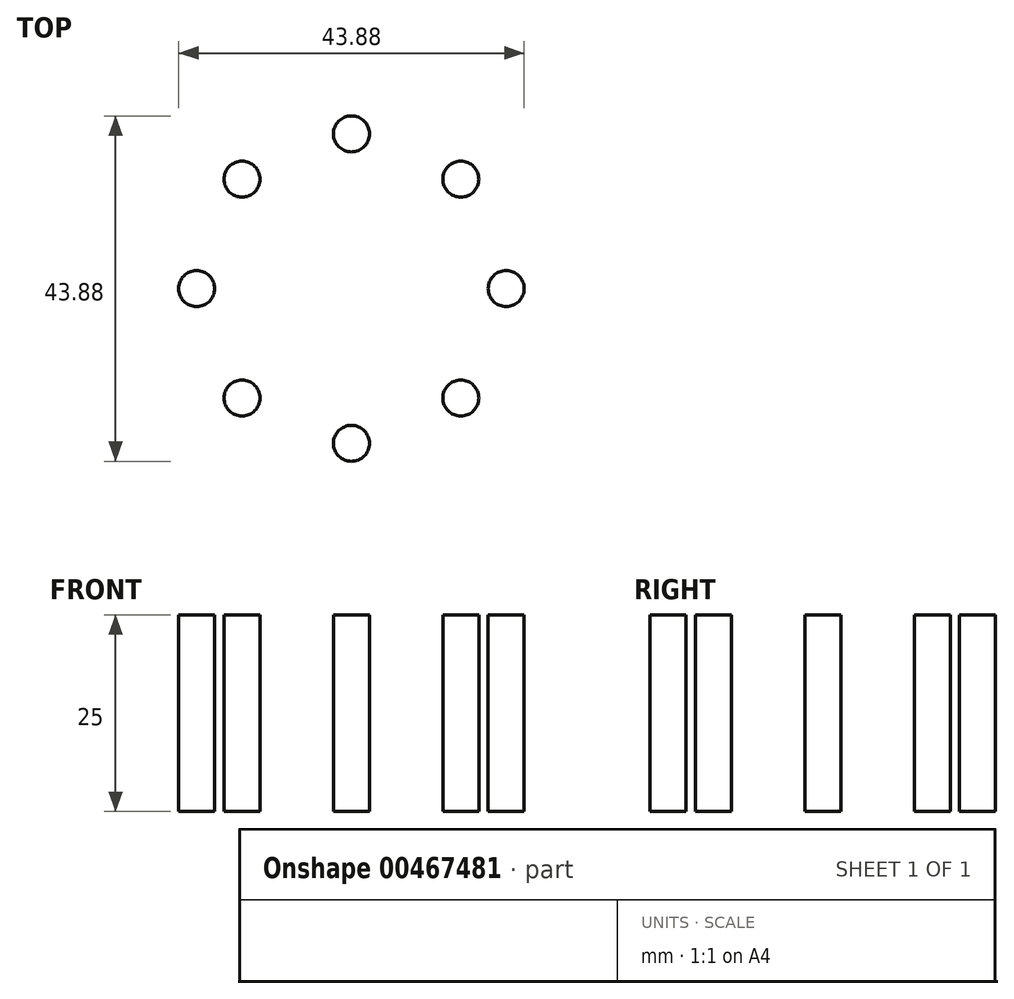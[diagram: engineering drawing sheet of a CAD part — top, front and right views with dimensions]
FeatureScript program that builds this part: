
annotation { "Feature Type Name" : "Feature", "Feature Type Description" : "" }
export const myFeature = defineFeature(function(context is Context, id is Id, definition is map)
    precondition{}
    {
        {
            var Q0;
            Q0=qCreatedBy(makeId("Top.planeOp"),FACE);
            var sketch = newSketch(context, id + "F0", { "sketchPlane" : qUnion([Q0])});
            skCircle(sketch, "E0", {"center": v(0, 0) * mm, "radius": 23.18 * mm});
            skCircle(sketch, "E1", {"center": v(0, 19.66) * mm, "radius": 2.29 * mm});
            skCircle(sketch, "E2.1.0", {"center": v(-13.9, 13.9) * mm, "radius": 2.29 * mm});
            skCircle(sketch, "E2.2.0", {"center": v(-19.66, 0) * mm, "radius": 2.29 * mm});
            skCircle(sketch, "E3.1.3.0", {"center": v(-13.9, -13.9) * mm, "radius": 2.29 * mm});
            skCircle(sketch, "E3.1.4.0", {"center": v(0, -19.66) * mm, "radius": 2.29 * mm});
            skCircle(sketch, "E3.1.5.0", {"center": v(13.9, -13.9) * mm, "radius": 2.29 * mm});
            skCircle(sketch, "E3.1.6.0", {"center": v(19.66, 0) * mm, "radius": 2.29 * mm});
            skCircle(sketch, "E3.1.7.0", {"center": v(13.9, 13.9) * mm, "radius": 2.29 * mm});
            skSolve(sketch);
        }
        {
            var Q0;
            Q0=makeQuery(id+"F0.imprint","IMPRINT",FACE,{"disambiguationData":[TD([[makeQuery(id+"F0.imprint","IMPRINT",EDGE,{"derivedFrom":sQuery(id+"F0.wireOp",EDGE,"E3.1.6.0")}),1.0]])]});
            var Q1;
            Q1=makeQuery(id+"F0.imprint","IMPRINT",FACE,{"disambiguationData":[TD([[makeQuery(id+"F0.imprint","IMPRINT",EDGE,{"derivedFrom":sQuery(id+"F0.wireOp",EDGE,"E3.1.7.0")}),1.0]])]});
            var Q2;
            Q2=makeQuery(id+"F0.imprint","IMPRINT",FACE,{"disambiguationData":[TD([[makeQuery(id+"F0.imprint","IMPRINT",EDGE,{"derivedFrom":sQuery(id+"F0.wireOp",EDGE,"E1")}),1.0]])]});
            var Q3;
            Q3=makeQuery(id+"F0.imprint","IMPRINT",FACE,{"disambiguationData":[TD([[makeQuery(id+"F0.imprint","IMPRINT",EDGE,{"derivedFrom":sQuery(id+"F0.wireOp",EDGE,"E2.1.0")}),1.0]])]});
            var Q4;
            Q4=makeQuery(id+"F0.imprint","IMPRINT",FACE,{"disambiguationData":[TD([[makeQuery(id+"F0.imprint","IMPRINT",EDGE,{"derivedFrom":sQuery(id+"F0.wireOp",EDGE,"E2.2.0")}),1.0]])]});
            var Q5;
            Q5=makeQuery(id+"F0.imprint","IMPRINT",FACE,{"disambiguationData":[TD([[makeQuery(id+"F0.imprint","IMPRINT",EDGE,{"derivedFrom":sQuery(id+"F0.wireOp",EDGE,"E3.1.3.0")}),1.0]])]});
            var Q6;
            Q6=makeQuery(id+"F0.imprint","IMPRINT",FACE,{"disambiguationData":[TD([[makeQuery(id+"F0.imprint","IMPRINT",EDGE,{"derivedFrom":sQuery(id+"F0.wireOp",EDGE,"E3.1.4.0")}),1.0]])]});
            var Q7;
            Q7=makeQuery(id+"F0.imprint","IMPRINT",FACE,{"disambiguationData":[TD([[makeQuery(id+"F0.imprint","IMPRINT",EDGE,{"derivedFrom":sQuery(id+"F0.wireOp",EDGE,"E3.1.5.0")}),1.0]])]});
            extrude(context, id + "F1", {"entities" : qUnion([Q0, Q1, Q2, Q3, Q4, Q5, Q6, Q7]), "depth" : 25 * mm});
        }
    });
